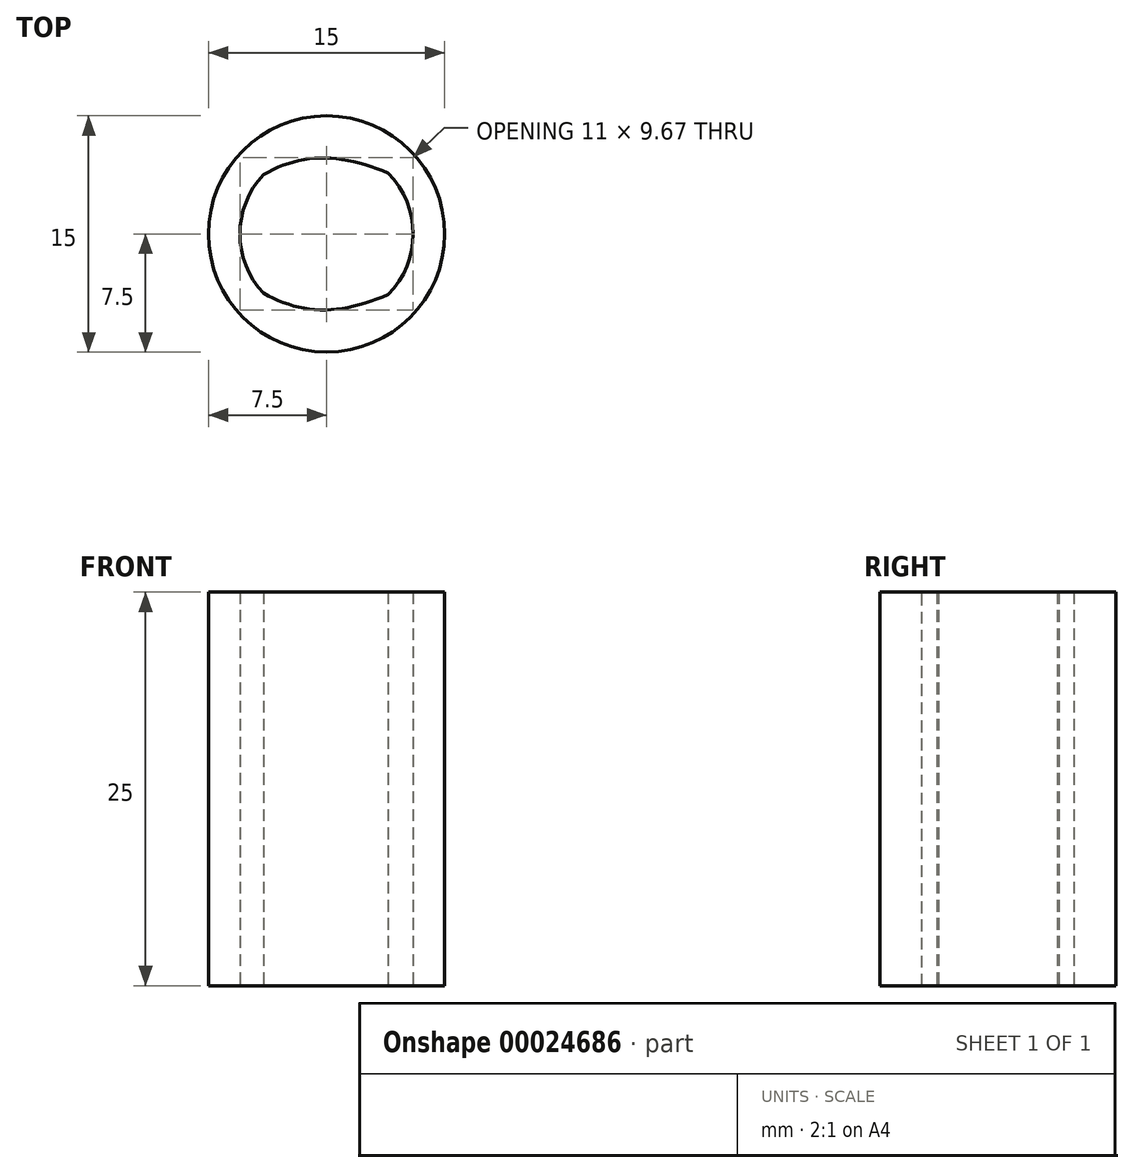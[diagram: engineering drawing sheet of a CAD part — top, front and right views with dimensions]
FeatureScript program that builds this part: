
annotation { "Feature Type Name" : "Feature", "Feature Type Description" : "" }
export const myFeature = defineFeature(function(context is Context, id is Id, definition is map)
    precondition{}
    {
        {
            var Q0;
            Q0=qCreatedBy(makeId("Top.planeOp"),FACE);
            var sketch = newSketch(context, id + "F0", { "sketchPlane" : qUnion([Q0])});
            skCircle(sketch, "E0", {"center": v(0, 0) * mm, "radius": 5.5 * mm});
            skFitSpline(sketch, "E1", {"points": [v(-8.47, 0.94) * mm, v(-5.5, 2.79) * mm, v(0, 4.83) * mm, v(6.82, 2.46) * mm, v(9.2, 1.34) * mm, v(0, 8.06) * mm, v(-6.75, 6.8) * mm, v(-8.47, 0.94) * mm]});
            skFitSpline(sketch, "E2.MirrorC", {"points": [v(-8.47, -0.94) * mm, v(-5.5, -2.79) * mm, v(0, -4.83) * mm, v(6.82, -2.46) * mm, v(9.2, -1.34) * mm, v(0, -8.06) * mm, v(-6.75, -6.8) * mm, v(-8.47, -0.94) * mm]});
            skCircle(sketch, "E3", {"center": v(0, 0) * mm, "radius": 7.5 * mm});
            skSolve(sketch);
        }
        {
            var Q0;
            {var subQ1=sQuery(id+"F0.wireOp",EDGE,"E1");var subQ6=sQuery(id+"F0.wireOp",EDGE,"E0");var subQ8=makeQuery(id+"F0.imprint","INTERSECT",VERTEX,{"disambiguationData":[OD(0.0)],"derivedFrom":[subQ6,subQ1]});Q0=makeQuery(id+"F0.imprint","IMPRINT",FACE,{"disambiguationData":[TD([[makeQuery(id+"F0.imprint","IMPRINT",EDGE,{"disambiguationData":[TD([[subQ8,1.0]])],"derivedFrom":subQ6}),-1.0]])]});}
            var Q1;
            {var subQ0=sQuery(id+"F0.wireOp",EDGE,"E3");var subQ1=sQuery(id+"F0.wireOp",EDGE,"E1");var subQ3=makeQuery(id+"F0.imprint","INTERSECT",VERTEX,{"disambiguationData":[OD(2.0)],"derivedFrom":[subQ1,subQ0]});Q1=makeQuery(id+"F0.imprint","IMPRINT",FACE,{"disambiguationData":[TD([[makeQuery(id+"F0.imprint","IMPRINT",EDGE,{"disambiguationData":[TD([[subQ3,-1.0]])],"derivedFrom":subQ1}),-1.0]])]});}
            var Q2;
            {var subQ0=sQuery(id+"F0.wireOp",EDGE,"E1");var subQ1=sQuery(id+"F0.wireOp",EDGE,"E0");var subQ3=makeQuery(id+"F0.imprint","INTERSECT",VERTEX,{"disambiguationData":[OD(0.0)],"derivedFrom":[subQ1,subQ0]});Q2=makeQuery(id+"F0.imprint","IMPRINT",FACE,{"disambiguationData":[TD([[makeQuery(id+"F0.imprint","IMPRINT",EDGE,{"disambiguationData":[TD([[subQ3,1.0]])],"derivedFrom":subQ1}),1.0]])]});}
            var Q3;
            {var subQ3=sQuery(id+"F0.wireOp",EDGE,"E1");var subQ5=sQuery(id+"F0.wireOp",EDGE,"E0");var subQ7=makeQuery(id+"F0.imprint","INTERSECT",VERTEX,{"disambiguationData":[OD(0.0)],"derivedFrom":[subQ5,subQ3]});Q3=makeQuery(id+"F0.imprint","IMPRINT",FACE,{"disambiguationData":[TD([[makeQuery(id+"F0.imprint","IMPRINT",EDGE,{"disambiguationData":[TD([[subQ7,-1.0]])],"derivedFrom":subQ5}),-1.0]])]});}
            var Q4;
            {var subQ3=sQuery(id+"F0.wireOp",EDGE,"E1");var subQ5=sQuery(id+"F0.wireOp",EDGE,"E0");var subQ7=makeQuery(id+"F0.imprint","INTERSECT",VERTEX,{"disambiguationData":[OD(1.0)],"derivedFrom":[subQ5,subQ3]});Q4=makeQuery(id+"F0.imprint","IMPRINT",FACE,{"disambiguationData":[TD([[makeQuery(id+"F0.imprint","IMPRINT",EDGE,{"disambiguationData":[TD([[subQ7,1.0]])],"derivedFrom":subQ5}),-1.0]])]});}
            var Q5;
            {var subQ1=sQuery(id+"F0.wireOp",EDGE,"E2.MirrorC");var subQ6=sQuery(id+"F0.wireOp",EDGE,"E0");var subQ8=makeQuery(id+"F0.imprint","INTERSECT",VERTEX,{"disambiguationData":[OD(0.0)],"derivedFrom":[subQ6,subQ1]});Q5=makeQuery(id+"F0.imprint","IMPRINT",FACE,{"disambiguationData":[TD([[makeQuery(id+"F0.imprint","IMPRINT",EDGE,{"disambiguationData":[TD([[subQ8,-1.0]])],"derivedFrom":subQ6}),-1.0]])]});}
            var Q6;
            {var subQ0=sQuery(id+"F0.wireOp",EDGE,"E2.MirrorC");var subQ1=sQuery(id+"F0.wireOp",EDGE,"E0");var subQ3=makeQuery(id+"F0.imprint","INTERSECT",VERTEX,{"disambiguationData":[OD(0.0)],"derivedFrom":[subQ1,subQ0]});Q6=makeQuery(id+"F0.imprint","IMPRINT",FACE,{"disambiguationData":[TD([[makeQuery(id+"F0.imprint","IMPRINT",EDGE,{"disambiguationData":[TD([[subQ3,-1.0]])],"derivedFrom":subQ1}),1.0]])]});}
            var Q7;
            {var subQ0=sQuery(id+"F0.wireOp",EDGE,"E3");var subQ1=sQuery(id+"F0.wireOp",EDGE,"E2.MirrorC");var subQ3=makeQuery(id+"F0.imprint","INTERSECT",VERTEX,{"disambiguationData":[OD(2.0)],"derivedFrom":[subQ1,subQ0]});Q7=makeQuery(id+"F0.imprint","IMPRINT",FACE,{"disambiguationData":[TD([[makeQuery(id+"F0.imprint","IMPRINT",EDGE,{"disambiguationData":[TD([[subQ3,-1.0]])],"derivedFrom":subQ1}),1.0]])]});}
            extrude(context, id + "F1", {"entities" : qUnion([Q0, Q1, Q2, Q3, Q4, Q5, Q6, Q7]), "depth" : 25 * mm});
        }
    });
